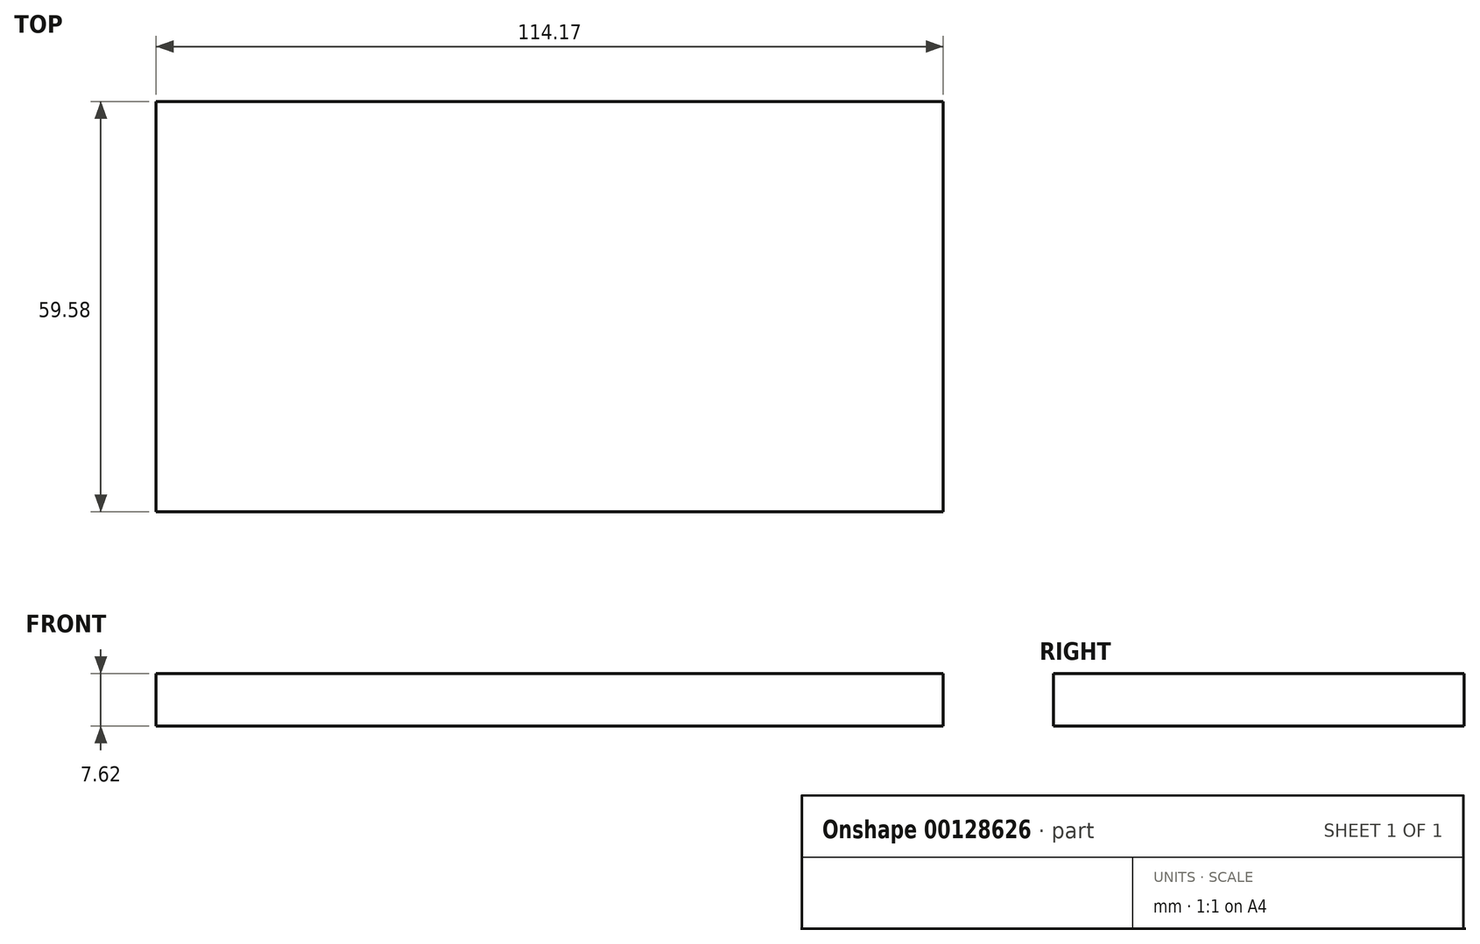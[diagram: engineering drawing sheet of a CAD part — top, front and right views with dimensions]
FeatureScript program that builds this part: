
annotation { "Feature Type Name" : "Feature", "Feature Type Description" : "" }
export const myFeature = defineFeature(function(context is Context, id is Id, definition is map)
    precondition{}
    {
        {
            var Q0;
            Q0=qCreatedBy(makeId("Top.planeOp"),FACE);
            var sketch = newSketch(context, id + "F0", { "sketchPlane" : qUnion([Q0])});
            skLineSegment(sketch, "E0.bottom", {"start": v(-58.33, 30.1) * mm, "end": v(55.84, 30.1) * mm});
            skLineSegment(sketch, "E0.top", {"start": v(-58.33, -29.48) * mm, "end": v(55.84, -29.48) * mm});
            skLineSegment(sketch, "E0.left", {"start": v(-58.33, 30.1) * mm, "end": v(-58.33, -29.48) * mm});
            skLineSegment(sketch, "E0.right", {"start": v(55.84, 30.1) * mm, "end": v(55.84, -29.48) * mm});
            skSolve(sketch);
        }
        {
            var Q0;
            Q0=makeQuery(id+"F0.imprint","IMPRINT",FACE,{"disambiguationData":[TD([[makeQuery(id+"F0.imprint","IMPRINT",EDGE,{"derivedFrom":sQuery(id+"F0.wireOp",EDGE,"E0.bottom")}),-1.0]])]});
            extrude(context, id + "F1", {"entities" : qUnion([Q0]), "depth" : 7.62 * mm});
        }
    });
